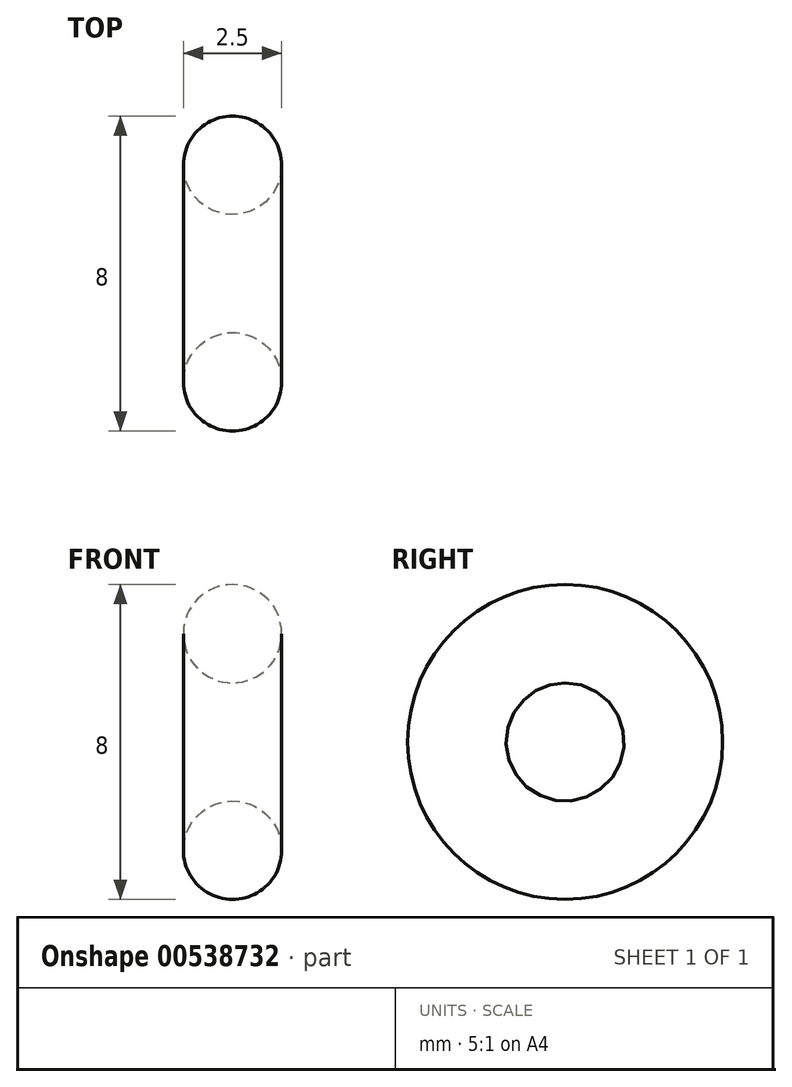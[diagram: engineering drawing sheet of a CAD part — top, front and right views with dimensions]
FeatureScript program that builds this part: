
annotation { "Feature Type Name" : "Feature", "Feature Type Description" : "" }
export const myFeature = defineFeature(function(context is Context, id is Id, definition is map)
    precondition{}
    {
        {
            var Q0;
            Q0=qCreatedBy(makeId("Front.planeOp"),FACE);
            var sketch = newSketch(context, id + "F0", { "sketchPlane" : qUnion([Q0])});
            skCircle(sketch, "E0", {"center": v(0, 2.75) * mm, "radius": 1.25 * mm});
            skLineSegment(sketch, "E1", {"start": v(0, 0) * mm, "end": v(39.06, 0) * mm, "construction": true});
            skSolve(sketch);
        }
        {
            var Q0;
            Q0=makeQuery(id+"F0.imprint","IMPRINT",FACE,{"disambiguationData":[TD([[makeQuery(id+"F0.imprint","IMPRINT",EDGE,{"derivedFrom":sQuery(id+"F0.wireOp",EDGE,"E0")}),1.0]])]});
            var Q1;
            Q1=sQuery(id+"F0.wireOp",EDGE,"E1");
            var Q2;
            Q2=sQuery(id+"F0.wireOp",EDGE,"E0");
            var Q3;
            Q3=sQuery(id+"F0.wireOp",EDGE,"E1");
            revolve(context, id + "F1", {"entities" : qUnion([Q0]), "surfaceEntities" : qUnion([Q1, Q2]), "axis" : qUnion([Q3]), "revolveType" : RevolveType.FULL});
        }
    });
